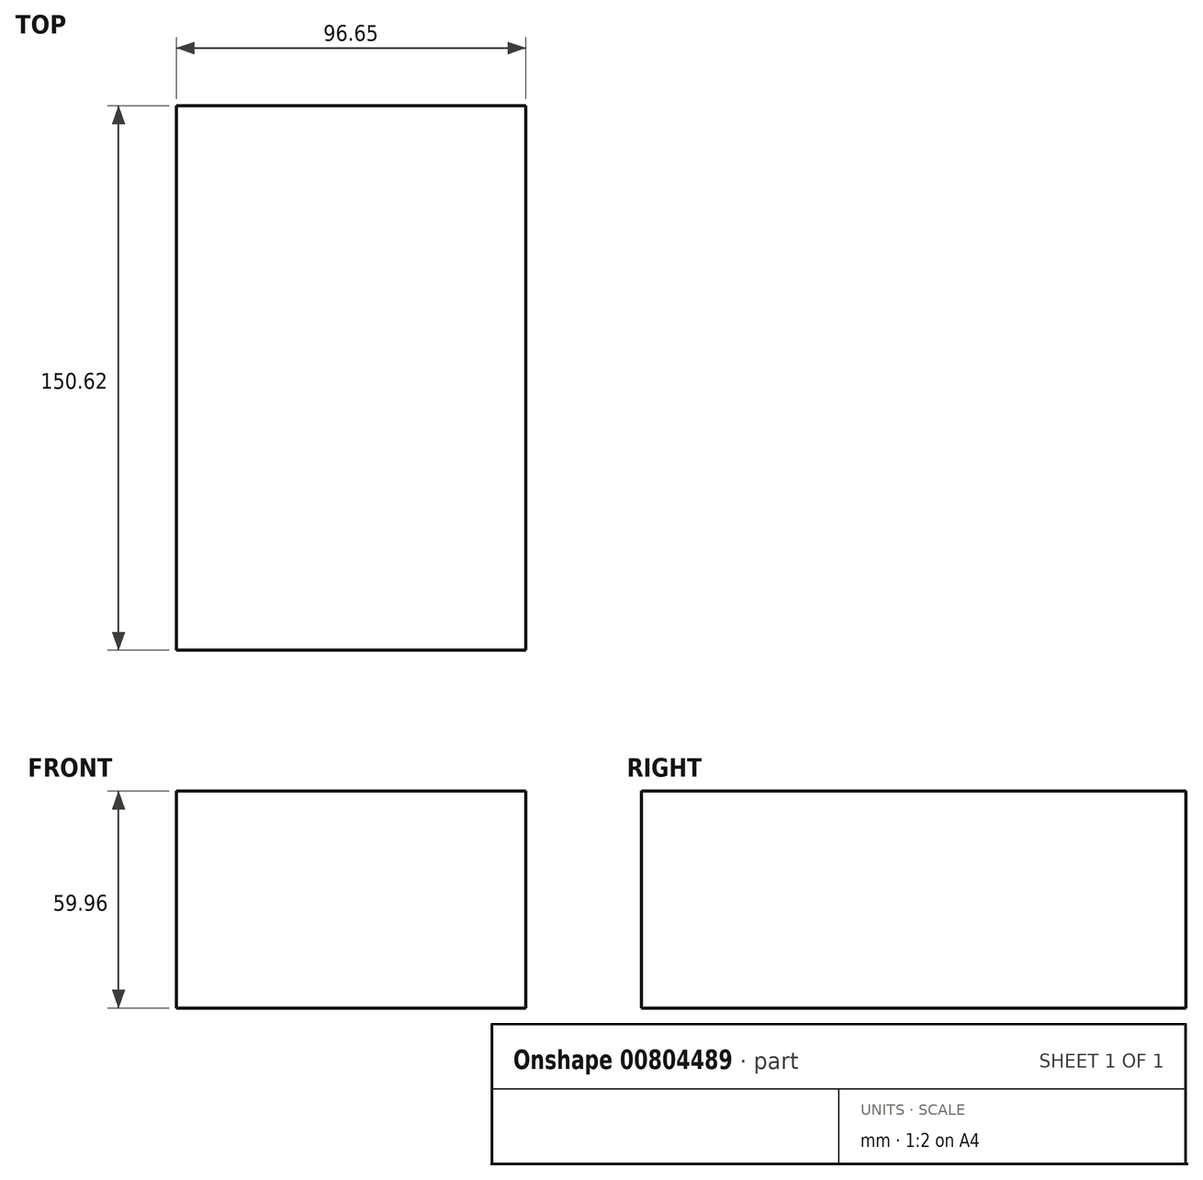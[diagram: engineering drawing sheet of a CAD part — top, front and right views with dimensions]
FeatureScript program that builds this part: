
annotation { "Feature Type Name" : "Feature", "Feature Type Description" : "" }
export const myFeature = defineFeature(function(context is Context, id is Id, definition is map)
    precondition{}
    {
        {
            var Q0;
            Q0=qCreatedBy(makeId("Front.planeOp"),FACE);
            var sketch = newSketch(context, id + "F0", { "sketchPlane" : qUnion([Q0])});
            skLineSegment(sketch, "E0.bottom", {"start": v(-49.17, 49) * mm, "end": v(47.48, 49) * mm});
            skLineSegment(sketch, "E0.top", {"start": v(-49.17, -10.96) * mm, "end": v(47.48, -10.96) * mm});
            skLineSegment(sketch, "E0.left", {"start": v(-49.17, 49) * mm, "end": v(-49.17, -10.96) * mm});
            skLineSegment(sketch, "E0.right", {"start": v(47.48, 49) * mm, "end": v(47.48, -10.96) * mm});
            skSolve(sketch);
        }
        {
            var Q0;
            Q0 = qSketchRegion(id + "F0", true);
            extrude(context, id + "F1", {"entities" : qUnion([Q0]), "depth" : 150.62 * mm, "offsetDistance" : 25.4 * mm});
        }
    });
